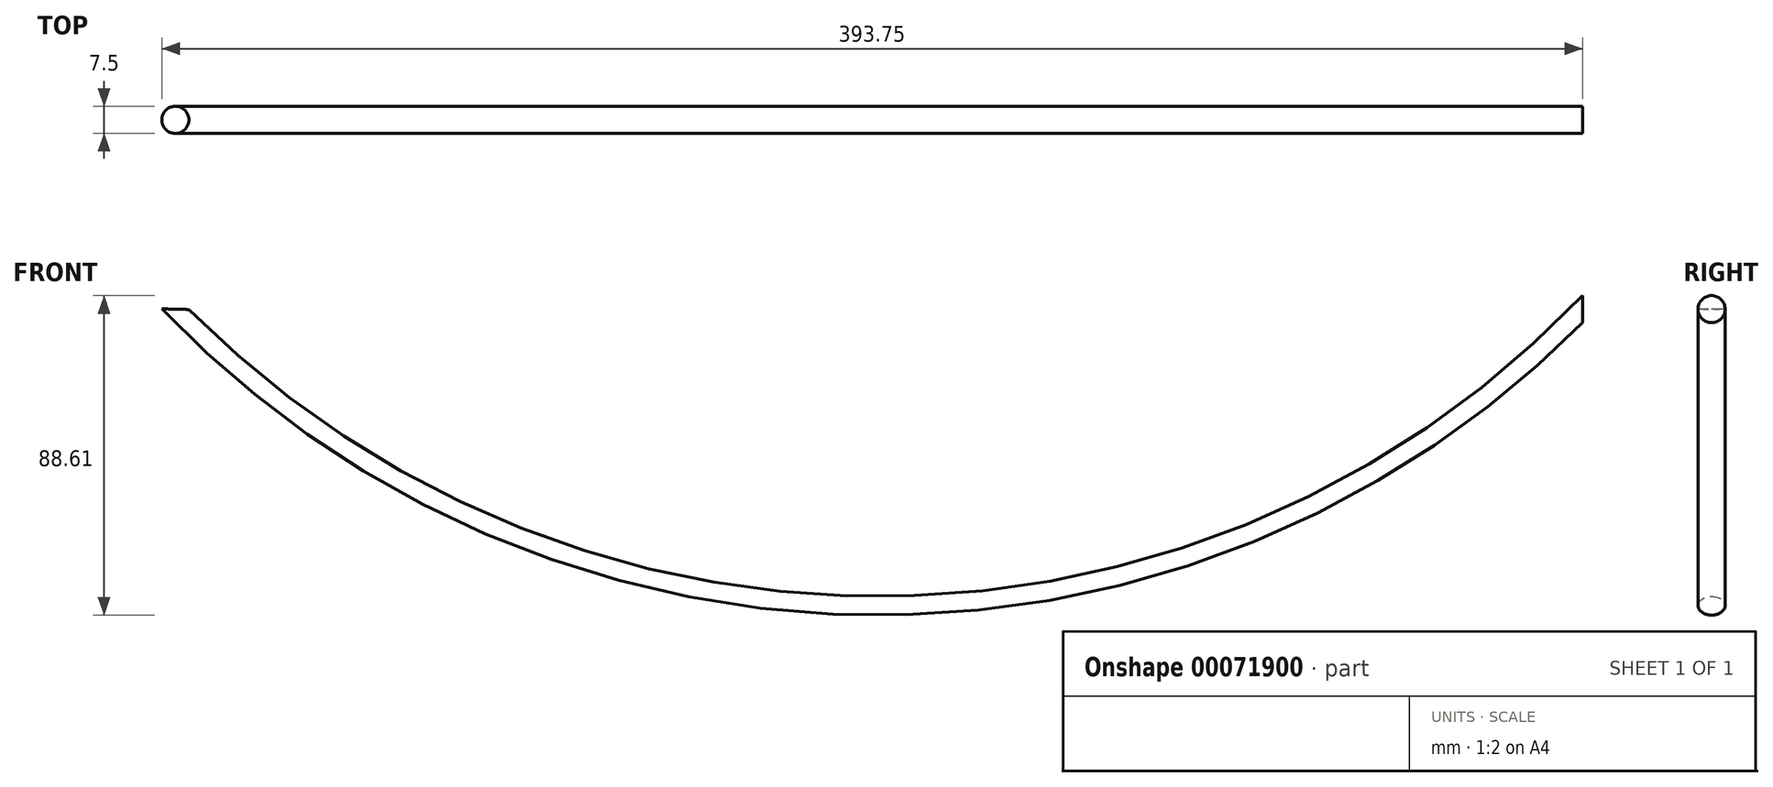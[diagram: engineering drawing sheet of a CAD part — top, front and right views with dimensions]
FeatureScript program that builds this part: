
annotation { "Feature Type Name" : "Feature", "Feature Type Description" : "" }
export const myFeature = defineFeature(function(context is Context, id is Id, definition is map)
    precondition{}
    {
        {
            var Q0;
            Q0=qCreatedBy(makeId("Front.planeOp"),FACE);
            var sketch = newSketch(context, id + "F0", { "sketchPlane" : qUnion([Q0])});
            skArc(sketch, "E0", {"start": v(-390, 0) * mm, "mid": v(-195, -82.23) * mm, "end": v(0, 0) * mm});
            skSolve(sketch);
        }
        {
            var Q0;
            Q0=qCreatedBy(makeId("Right.planeOp"),FACE);
            var sketch = newSketch(context, id + "F1", { "sketchPlane" : qUnion([Q0])});
            skCircle(sketch, "E1", {"center": v(0, 0) * mm, "radius": 3.75 * mm});
            skSolve(sketch);
        }
        {
            var Q0;
            Q0 = qSketchRegion(id + "F1", true);
            var Q1;
            Q1 = qConstructionFilter(qBodyType(qCreatedBy(id + "F0" ,EDGE), BodyType.WIRE), ConstructionObject.NO);
            sweep(context, id + "F2", {"profiles" : qUnion([Q0]), "path" : qUnion([Q1])});
        }
    });
